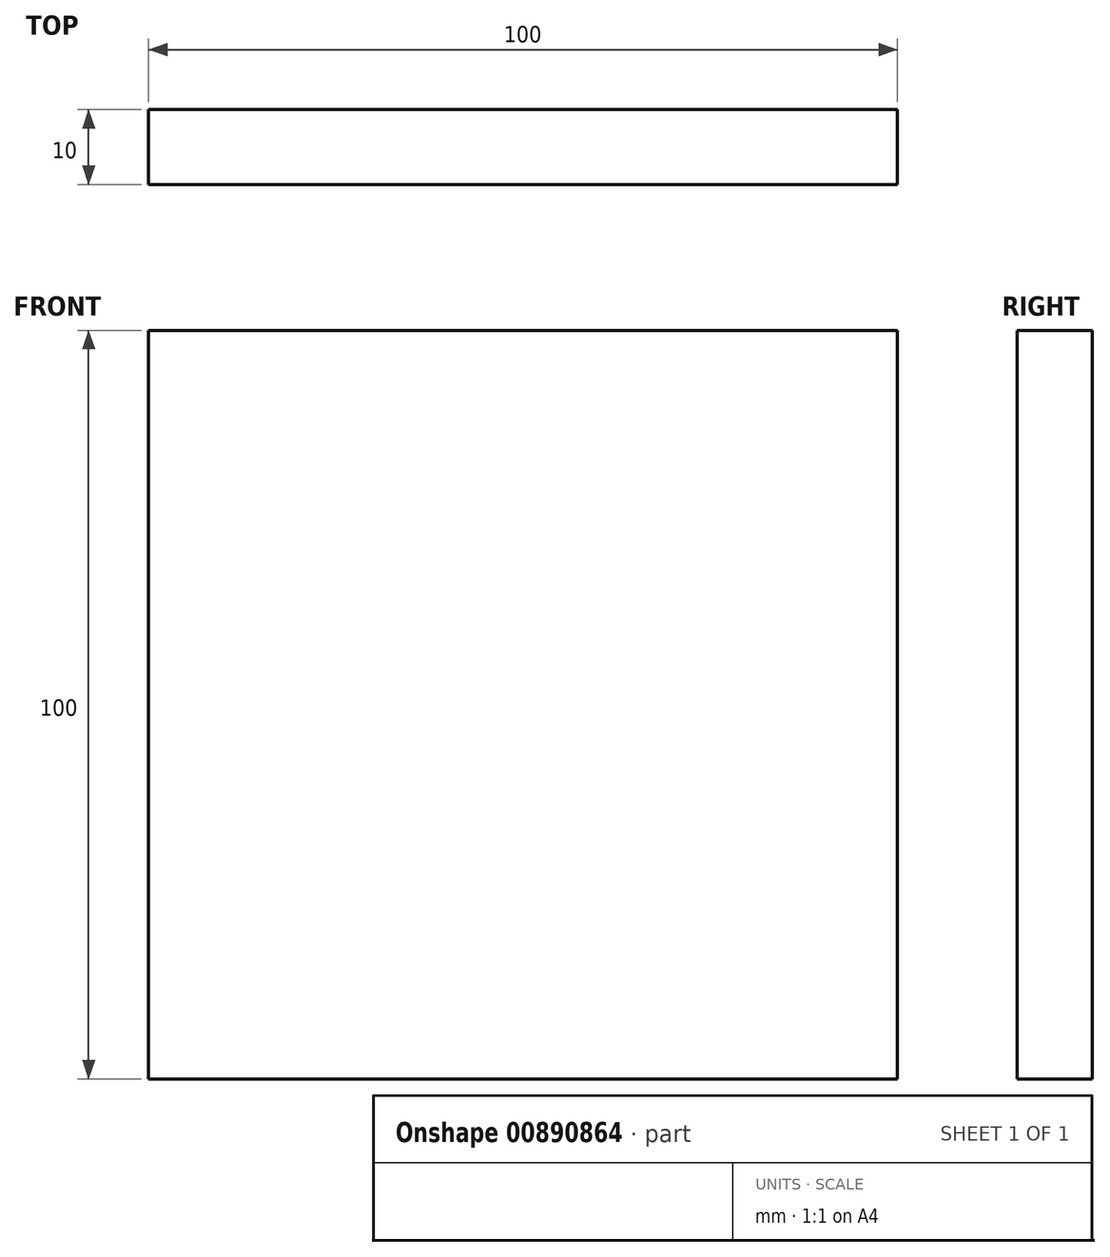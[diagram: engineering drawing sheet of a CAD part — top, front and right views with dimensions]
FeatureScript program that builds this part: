
annotation { "Feature Type Name" : "Feature", "Feature Type Description" : "" }
export const myFeature = defineFeature(function(context is Context, id is Id, definition is map)
    precondition{}
    {
        {
            var Q0;
            Q0=qCreatedBy(makeId("Front.planeOp"),FACE);
            var sketch = newSketch(context, id + "F0", { "sketchPlane" : qUnion([Q0])});
            skLineSegment(sketch, "E0.bottom", {"start": v(50, -50) * mm, "end": v(-50, -50) * mm});
            skLineSegment(sketch, "E0.top", {"start": v(50, 50) * mm, "end": v(-50, 50) * mm});
            skLineSegment(sketch, "E0.left", {"start": v(50, -50) * mm, "end": v(50, 50) * mm});
            skLineSegment(sketch, "E0.right", {"start": v(-50, -50) * mm, "end": v(-50, 50) * mm});
            skPoint(sketch, "E0.middle", {"position": v(0, 0) * mm});
            skSolve(sketch);
        }
        {
            var Q0;
            Q0=makeQuery(id+"F0.imprint","IMPRINT",FACE,{"disambiguationData":[TD([[makeQuery(id+"F0.imprint","IMPRINT",EDGE,{"derivedFrom":sQuery(id+"F0.wireOp",EDGE,"E0.bottom")}),-1.0]])]});
            extrude(context, id + "F1", {"entities" : qUnion([Q0]), "depth" : 10 * mm, "offsetDistance" : 25 * mm});
        }
    });
